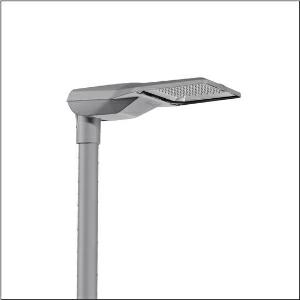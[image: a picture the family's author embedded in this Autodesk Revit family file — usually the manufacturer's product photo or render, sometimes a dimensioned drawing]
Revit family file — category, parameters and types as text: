
# Revit family: streetlight_sl_21_iq_midi___pl52_5xe3h41d08mb_c975
name_source: partatom
category: Lighting Fixtures
units: mm (PartAtom-declared; Revit-internal decimal feet)

## family parameters
Cut with Voids When Loaded = No
Host = Face
Light Source = No
Part Type = Normal
Room Calculation Point = No
Round Connector Dimension = Use Diameter
Shared = No

## types (1)
- --- (1 x LED, 20000 lm, 146.7 W, 4000K)
    Apparent Load = 147 VA
    CIE Flux Codes = 27 59 98 100 100
    Color Rendering = 70
    Color Temperature = 4000K
    Default Elevation = 1800 mm
    Description = Streetlight SL 21 iQ midi, mast luminaire, primary light control with lens, of PMMA, primary optical cover: cover, of toughened safety glass, transparent, light distribution: PL52, light emission: direct distribution, primary light characteristic: asymmetric, installation type: post-top, side-entry, LED, High Power LED, rated luminous flux: 20.000lm, luminous efficacy: 136lm/W, light colour: 740, colour temperature: 4000K, control gear: iQ-Comfort, control: Auto-Match, Temp-Guard, Lumen-Switch, Night-Set, Smart-Wire, Light-Fading, Desk-Remote (wireless, voltage-free reading and setting of iQ features in the workshop via application-optimized NFC function/RFID function), optimised constant luminous flux control (CLO 2.0), pre-setting: linear dimming characteristic, mains connection: 230..240V, AC, 50/60Hz, start of lifetime: 147W, end of service life: 161W, reduction: 62W, luminaire housing, of diecast aluminium, powder-coated, Siteco® metallic grey (DB 702S), corrosivity category C5 high according to DIN EN ISO 12944, please order mast flange separately, inclination adjustable: 0°, 5°, 10°, 15°, sealing non-destructively replaceable, multi-level sealing system, length: 644mm, width: 335mm, height: 110mm, mast flange for spigot size: 42mm (side-entry): 5XC10008XM4, 60/48mm (side-entry/post-top): 5XC10108XM2, 76/60mm (side-entry/post-top): 5XC10108XM1, mounting height: 4..8m, protection rating (complete): IP66, insulation class (complete): insulation class II (safety insulation), certification: CE, ENEC, ENEC+, VDE, impact resistance: IK10, permissible operating ambient temperature for outdoor applications: -40..+50°C, standard-compliant lighting for roads and squares, packaging unit: 1 piece

Light Distribution: PL52
    Height = 111 mm
    Lamp = 1 x LED
    Lamp Light Flux = 20000 lm
    Lamp Power = 146.7 W
    Lamp count = 1
    Length = 644 mm
    Luminous efficacy = 136 lm/W
    Manufacturer = Siteco
    ModVariant = No
    Model = 5XE3H41D08MB
    Number of Poles = 1
    OnlyDefault = Yes
    Power Factor = 1
    Product Name = Streetlight SL 21 iQ midi | PL52
    Product group = mast luminaire | pylon top
    ProductGroupID = 6100
    Protection Class = Protection class II
    Protection Degree = IP 66
    RLX_Detail_Level = 1
    RLX_Emergency_Light_Flux = 0 lm
    RLX_Emergency_Type = 0
    RLX_Emergency_Type_DB = No
    RlxData = <blob elided: 36569 chars, md5=41922ad2>
    Socket = socket
    Standby Power = 0 W
    System Light Flux = 20000 lm
    System Power = 147 W
    Type Comments = factory setting: luminous flux: 100 % | dim-lin: 254 | 753 mA
    Type Image = l_1004298.jpg
    URL = http://relux.com
    VarID = @adj_191987
    Voltage = 0 V
    Weight = 0.00 kg
    Width = 336 mm

## geometry (parser evidence)
native form markers: Blend x4, Sweep x12
no freeform markers — native parametric forms only
